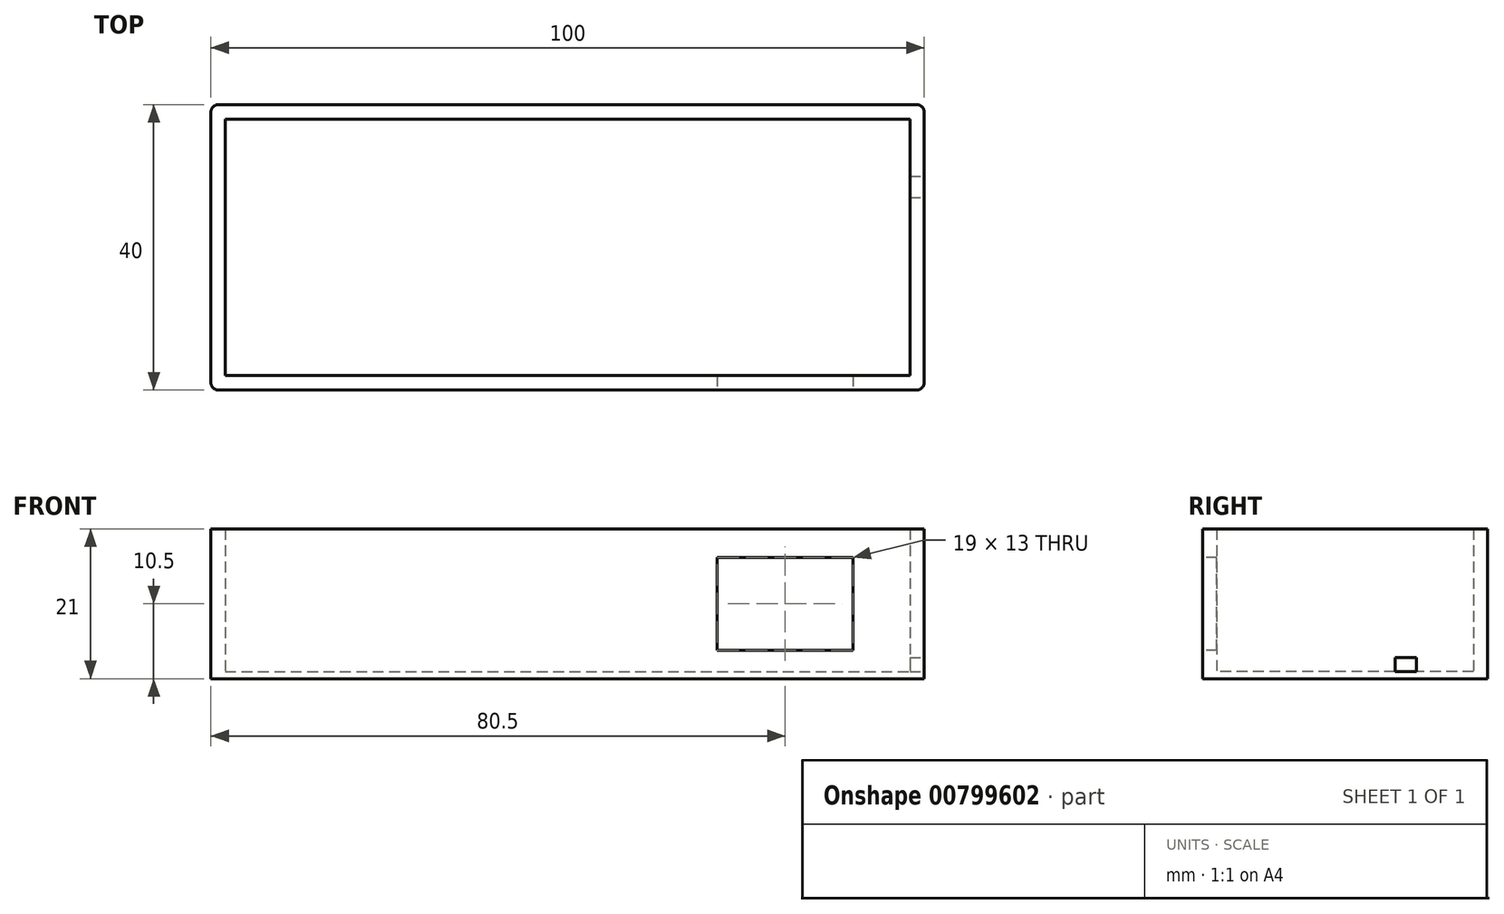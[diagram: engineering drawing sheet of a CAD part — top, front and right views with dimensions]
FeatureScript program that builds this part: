
annotation { "Feature Type Name" : "Feature", "Feature Type Description" : "" }
export const myFeature = defineFeature(function(context is Context, id is Id, definition is map)
    precondition{}
    {
        {
            var Q0;
            Q0=qCreatedBy(makeId("Top.planeOp"),FACE);
            var sketch = newSketch(context, id + "F0", { "sketchPlane" : qUnion([Q0])});
            skLineSegment(sketch, "E0.bottom", {"start": v(0, 0) * mm, "end": v(100, 0) * mm});
            skLineSegment(sketch, "E0.top", {"start": v(0, 40) * mm, "end": v(100, 40) * mm});
            skLineSegment(sketch, "E0.left", {"start": v(0, 0) * mm, "end": v(0, 40) * mm});
            skLineSegment(sketch, "E0.right", {"start": v(100, 0) * mm, "end": v(100, 40) * mm});
            skSolve(sketch);
        }
        {
            var Q0;
            Q0=makeQuery(id+"F0.imprint","IMPRINT",FACE,{"disambiguationData":[TD([[makeQuery(id+"F0.imprint","IMPRINT",EDGE,{"derivedFrom":sQuery(id+"F0.wireOp",EDGE,"E0.bottom")}),1.0]])]});
            extrude(context, id + "F1", {"entities" : qUnion([Q0]), "depth" : 1 * mm, "offsetDistance" : 25 * mm});
        }
        {
            var Q0;
            Q0=makeQuery(id+"F1.opExtrude","CAP_FACE",FACE,{"disambiguationData":[OSD([sQuery(id+"F0.wireOp",EDGE,"E0.bottom"),sQuery(id+"F0.wireOp",EDGE,"E0.top"),sQuery(id+"F0.wireOp",EDGE,"E0.left"),sQuery(id+"F0.wireOp",EDGE,"E0.right")])],"isStart":false});
            var sketch = newSketch(context, id + "F2", { "sketchPlane" : qUnion([Q0])});
            skLineSegment(sketch, "E1.bottom", {"start": v(2, 38) * mm, "end": v(98, 38) * mm});
            skLineSegment(sketch, "E1.top", {"start": v(2, 2) * mm, "end": v(98, 2) * mm});
            skLineSegment(sketch, "E1.left", {"start": v(2, 38) * mm, "end": v(2, 2) * mm});
            skLineSegment(sketch, "E1.right", {"start": v(98, 38) * mm, "end": v(98, 2) * mm});
            skSolve(sketch);
        }
        {
            var Q0;
            Q0=makeQuery(id+"F2.imprint","IMPRINT",FACE,{"disambiguationData":[TD([[makeQuery(id+"F2.imprint","IMPRINT",EDGE,{"derivedFrom":sQuery(id+"F2.wireOp",EDGE,"E1.bottom")}),1.0]])]});
            extrude(context, id + "F3", {"entities" : qUnion([Q0]), "operationType" : NewBodyOperationType.ADD, "depth" : 20 * mm, "offsetDistance" : 25 * mm});
        }
        {
            var Q0;
            {var subQ0=sQuery(id+"F0.wireOp",EDGE,"E0.right");Q0=makeQuery(id+"F3.boolean.opBoolean","MERGE",FACE,{"derivedFrom":[makeQuery(id+"F1.opExtrude","SWEPT_FACE",FACE,{"disambiguationData":[OSD([subQ0])]}),makeQuery(id+"F3.opExtrude","SWEPT_FACE",FACE,{"disambiguationData":[OSD([subQ0])]})]});}
            var sketch = newSketch(context, id + "F4", { "sketchPlane" : qUnion([Q0])});
            skLineSegment(sketch, "E2.bottom", {"start": v(27, 3) * mm, "end": v(30, 3) * mm});
            skLineSegment(sketch, "E2.top", {"start": v(27, 1) * mm, "end": v(30, 1) * mm});
            skLineSegment(sketch, "E2.left", {"start": v(27, 3) * mm, "end": v(27, 1) * mm});
            skLineSegment(sketch, "E2.right", {"start": v(30, 3) * mm, "end": v(30, 1) * mm});
            skSolve(sketch);
        }
        {
            var Q0;
            Q0=makeQuery(id+"F4.imprint","IMPRINT",FACE,{"disambiguationData":[TD([[makeQuery(id+"F4.imprint","IMPRINT",EDGE,{"derivedFrom":sQuery(id+"F4.wireOp",EDGE,"E2.bottom")}),-1.0]])]});
            extrude(context, id + "F5", {"entities" : qUnion([Q0]), "operationType" : NewBodyOperationType.REMOVE, "oppositeDirection" : true, "depth" : 25 * mm, "offsetDistance" : 25 * mm});
        }
        {
            var Q0;
            {var subQ0=sQuery(id+"F0.wireOp",EDGE,"E0.bottom");Q0=makeQuery(id+"F3.boolean.opBoolean","MERGE",FACE,{"derivedFrom":[makeQuery(id+"F1.opExtrude","SWEPT_FACE",FACE,{"disambiguationData":[OSD([subQ0])]}),makeQuery(id+"F3.opExtrude","SWEPT_FACE",FACE,{"disambiguationData":[OSD([subQ0])]})]});}
            var sketch = newSketch(context, id + "F6", { "sketchPlane" : qUnion([Q0])});
            skLineSegment(sketch, "E3.bottom", {"start": v(71, 17) * mm, "end": v(90, 17) * mm});
            skLineSegment(sketch, "E3.top", {"start": v(71, 4) * mm, "end": v(90, 4) * mm});
            skLineSegment(sketch, "E3.left", {"start": v(71, 17) * mm, "end": v(71, 4) * mm});
            skLineSegment(sketch, "E3.right", {"start": v(90, 17) * mm, "end": v(90, 4) * mm});
            skSolve(sketch);
        }
        {
            var Q0;
            Q0=makeQuery(id+"F6.imprint","IMPRINT",FACE,{"disambiguationData":[TD([[makeQuery(id+"F6.imprint","IMPRINT",EDGE,{"derivedFrom":sQuery(id+"F6.wireOp",EDGE,"E3.bottom")}),-1.0]])]});
            extrude(context, id + "F7", {"entities" : qUnion([Q0]), "operationType" : NewBodyOperationType.REMOVE, "oppositeDirection" : true, "depth" : 25 * mm, "offsetDistance" : 25 * mm});
        }
        {
            var Q0;
            {var subQ0=sQuery(id+"F0.wireOp",EDGE,"E0.left");var subQ1=sQuery(id+"F0.wireOp",EDGE,"E0.bottom");Q0=makeQuery(id+"F3.boolean.opBoolean","MERGE",EDGE,{"derivedFrom":[makeQuery(id+"F1.opExtrude","SWEPT_EDGE",EDGE,{"disambiguationData":[OSD([subQ1,subQ0])]}),makeQuery(id+"F3.opExtrude","SWEPT_EDGE",EDGE,{"disambiguationData":[OSD([subQ1,subQ0])]})]});}
            var Q1;
            {var subQ0=sQuery(id+"F0.wireOp",EDGE,"E0.right");var subQ1=sQuery(id+"F0.wireOp",EDGE,"E0.bottom");Q1=makeQuery(id+"F3.boolean.opBoolean","MERGE",EDGE,{"derivedFrom":[makeQuery(id+"F1.opExtrude","SWEPT_EDGE",EDGE,{"disambiguationData":[OSD([subQ1,subQ0])]}),makeQuery(id+"F3.opExtrude","SWEPT_EDGE",EDGE,{"disambiguationData":[OSD([subQ1,subQ0])]})]});}
            var Q2;
            {var subQ0=sQuery(id+"F0.wireOp",EDGE,"E0.right");var subQ1=sQuery(id+"F0.wireOp",EDGE,"E0.top");Q2=makeQuery(id+"F3.boolean.opBoolean","MERGE",EDGE,{"derivedFrom":[makeQuery(id+"F1.opExtrude","SWEPT_EDGE",EDGE,{"disambiguationData":[OSD([subQ1,subQ0])]}),makeQuery(id+"F3.opExtrude","SWEPT_EDGE",EDGE,{"disambiguationData":[OSD([subQ1,subQ0])]})]});}
            var Q3;
            {var subQ0=sQuery(id+"F0.wireOp",EDGE,"E0.left");var subQ1=sQuery(id+"F0.wireOp",EDGE,"E0.top");Q3=makeQuery(id+"F3.boolean.opBoolean","MERGE",EDGE,{"derivedFrom":[makeQuery(id+"F1.opExtrude","SWEPT_EDGE",EDGE,{"disambiguationData":[OSD([subQ1,subQ0])]}),makeQuery(id+"F3.opExtrude","SWEPT_EDGE",EDGE,{"disambiguationData":[OSD([subQ1,subQ0])]})]});}
            fillet(context, id + "F8", {"entities" : qUnion([Q0, Q1, Q2, Q3]), "radius" : 1 * mm, "tangentPropagation" : true, "allowEdgeOverflow" : false});
        }
    });
